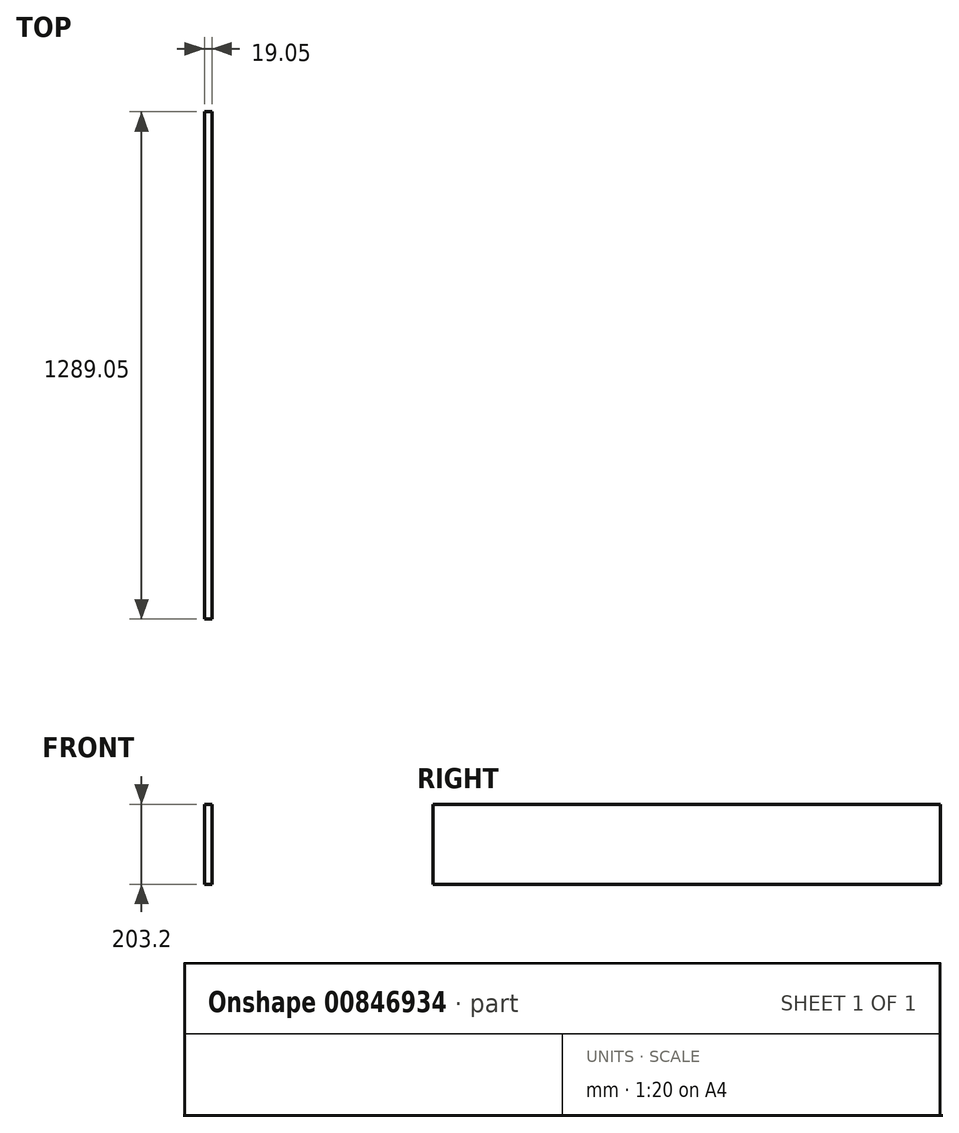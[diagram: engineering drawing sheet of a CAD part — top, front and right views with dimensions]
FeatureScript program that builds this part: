
annotation { "Feature Type Name" : "Feature", "Feature Type Description" : "" }
export const myFeature = defineFeature(function(context is Context, id is Id, definition is map)
    precondition{}
    {
        {
            var Q0;
            Q0=qCreatedBy(makeId("Right.planeOp"),FACE);
            var sketch = newSketch(context, id + "F0", { "sketchPlane" : qUnion([Q0])});
            skLineSegment(sketch, "E0.bottom", {"start": v(-1289.05, 0) * mm, "end": v(0, 0) * mm});
            skLineSegment(sketch, "E0.top", {"start": v(-1289.05, -203.2) * mm, "end": v(0, -203.2) * mm});
            skLineSegment(sketch, "E0.left", {"start": v(-1289.05, 0) * mm, "end": v(-1289.05, -203.2) * mm});
            skLineSegment(sketch, "E0.right", {"start": v(0, 0) * mm, "end": v(0, -203.2) * mm});
            skSolve(sketch);
        }
        {
            var Q0;
            Q0=makeQuery(id+"F0.imprint","IMPRINT",FACE,{"disambiguationData":[TD([[makeQuery(id+"F0.imprint","IMPRINT",EDGE,{"derivedFrom":sQuery(id+"F0.wireOp",EDGE,"E0.bottom")}),-1.0]])]});
            extrude(context, id + "F1", {"entities" : qUnion([Q0]), "depth" : 19.05 * mm, "offsetDistance" : 25.4 * mm});
        }
    });
